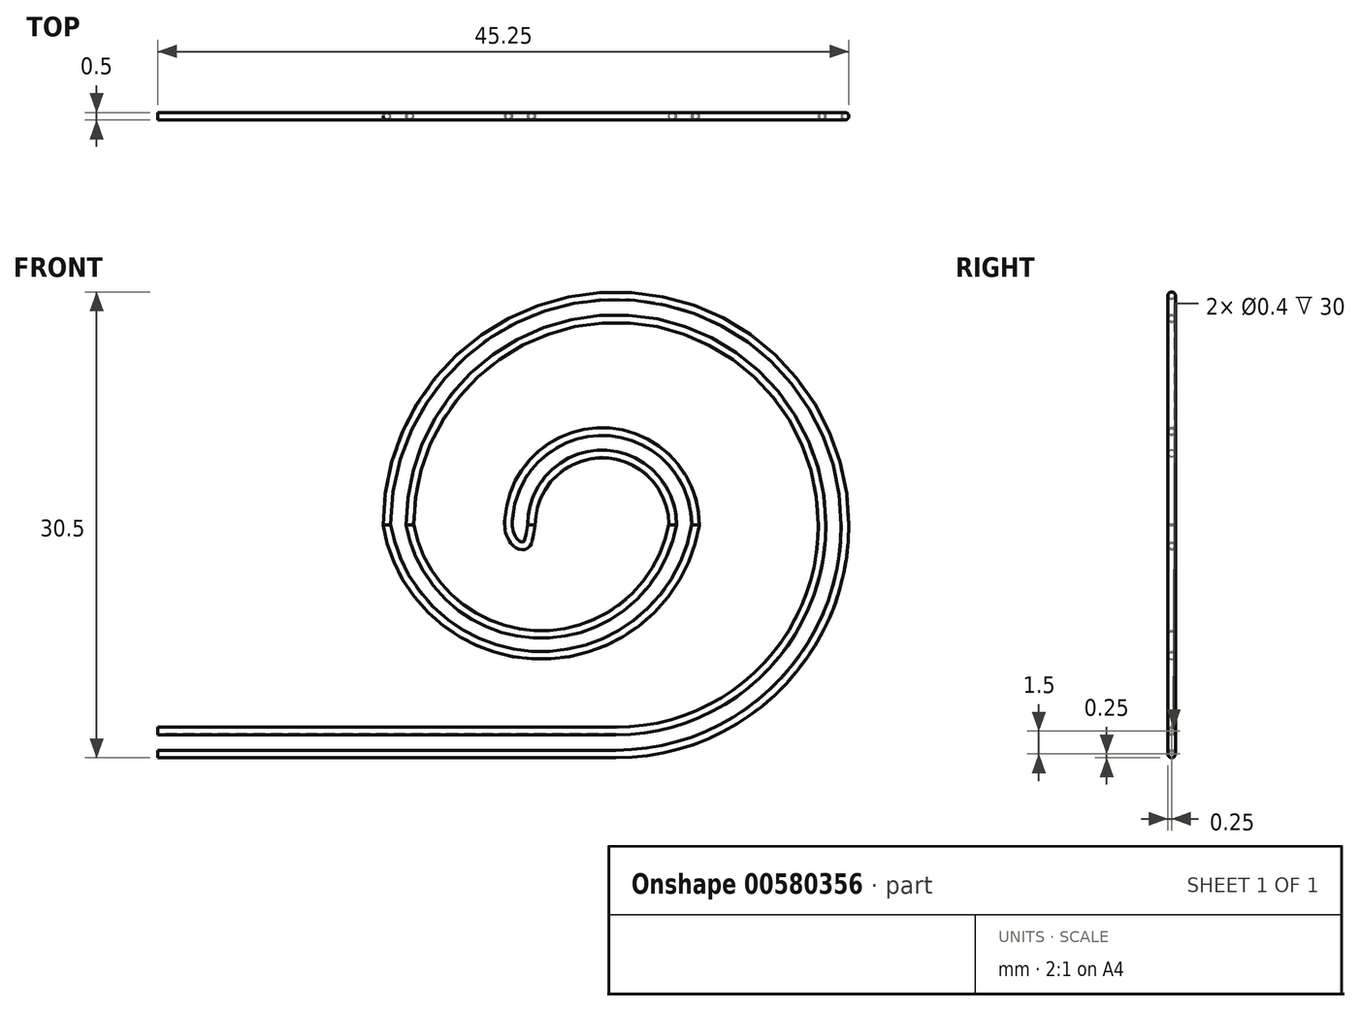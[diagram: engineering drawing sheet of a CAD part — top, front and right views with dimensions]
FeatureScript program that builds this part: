
annotation { "Feature Type Name" : "Feature", "Feature Type Description" : "" }
export const myFeature = defineFeature(function(context is Context, id is Id, definition is map)
    precondition{}
    {
        {
            var Q0;
            Q0=qCreatedBy(makeId("Front.planeOp"),FACE);
            var sketch = newSketch(context, id + "F0", { "sketchPlane" : qUnion([Q0])});
            skLineSegment(sketch, "E0", {"start": v(0, 0) * mm, "end": v(30, 0) * mm});
            skPoint(sketch, "E1", {"position": v(45, 15) * mm});
            skPoint(sketch, "E2", {"position": v(30, 0) * mm});
            skArc(sketch, "E3", {"start": v(30, 0) * mm, "mid": v(40.6, 4.4) * mm, "end": v(45, 15) * mm});
            skLineSegment(sketch, "E4", {"start": v(45, 15) * mm, "end": v(45, 15) * mm});
            skArc(sketch, "E5", {"start": v(45, 15) * mm, "mid": v(30, 30) * mm, "end": v(15, 15) * mm});
            skPoint(sketch, "E6", {"position": v(22.5, 15) * mm});
            skPoint(sketch, "E7", {"position": v(26.25, 15) * mm});
            skArc(sketch, "E8", {"start": v(43.5, 15) * mm, "mid": v(30, 28.5) * mm, "end": v(16.5, 15) * mm});
            skArc(sketch, "E9", {"start": v(30, 1.5) * mm, "mid": v(39.55, 5.45) * mm, "end": v(43.5, 15) * mm});
            skLineSegment(sketch, "E10", {"start": v(30, 1.5) * mm, "end": v(0, 1.5) * mm});
            skPoint(sketch, "E11", {"position": v(36, 15) * mm});
            skArc(sketch, "E12", {"start": v(15, 15) * mm, "mid": v(25.1, 6.45) * mm, "end": v(35.21, 15) * mm});
            skArc(sketch, "E13", {"start": v(16.5, 15) * mm, "mid": v(25.1, 7.82) * mm, "end": v(33.71, 15) * mm});
            skArc(sketch, "E14", {"start": v(35.21, 15) * mm, "mid": v(29.09, 21.1) * mm, "end": v(22.96, 15) * mm});
            skArc(sketch, "E15", {"start": v(33.71, 15) * mm, "mid": v(29.09, 19.64) * mm, "end": v(24.46, 15) * mm});
            skFitSpline(sketch, "E16", {"points": [v(22.96, 15) * mm, v(23.98, 13.63) * mm, v(24.46, 15) * mm], "startDerivative": vector(0, -5.38) * mm, "endDerivative": vector(0.78, 4.18) * mm});
            skSolve(sketch);
        }
        {
            var Q0;
            Q0=qCreatedBy(makeId("Right.planeOp"),FACE);
            var sketch = newSketch(context, id + "F1", { "sketchPlane" : qUnion([Q0])});
            skCircle(sketch, "E17", {"center": v(0, 0) * mm, "radius": 0.25 * mm});
            skCircle(sketch, "E18", {"center": v(0, 0) * mm, "radius": 0.2 * mm});
            skSolve(sketch);
        }
        {
            var Q0;
            Q0 = qSketchRegion(id + "F1", true);
            var Q1;
            Q1=sQuery(id+"F0.wireOp",EDGE,"E0");
            var Q2;
            Q2=sQuery(id+"F0.wireOp",EDGE,"E3");
            var Q3;
            Q3=sQuery(id+"F0.wireOp",EDGE,"E5");
            var Q4;
            Q4=sQuery(id+"F0.wireOp",EDGE,"E12");
            var Q5;
            Q5=sQuery(id+"F0.wireOp",EDGE,"E14");
            var Q6;
            Q6=sQuery(id+"F0.wireOp",EDGE,"E16");
            var Q7;
            Q7=sQuery(id+"F0.wireOp",EDGE,"E15");
            var Q8;
            Q8=sQuery(id+"F0.wireOp",EDGE,"E13");
            var Q9;
            Q9=sQuery(id+"F0.wireOp",EDGE,"E8");
            var Q10;
            Q10=sQuery(id+"F0.wireOp",EDGE,"E9");
            var Q11;
            Q11=sQuery(id+"F0.wireOp",EDGE,"E10");
            sweep(context, id + "F2", {"profiles" : qUnion([Q0]), "path" : qUnion([Q1, Q2, Q3, Q4, Q5, Q6, Q7, Q8, Q9, Q10, Q11])});
        }
    });
